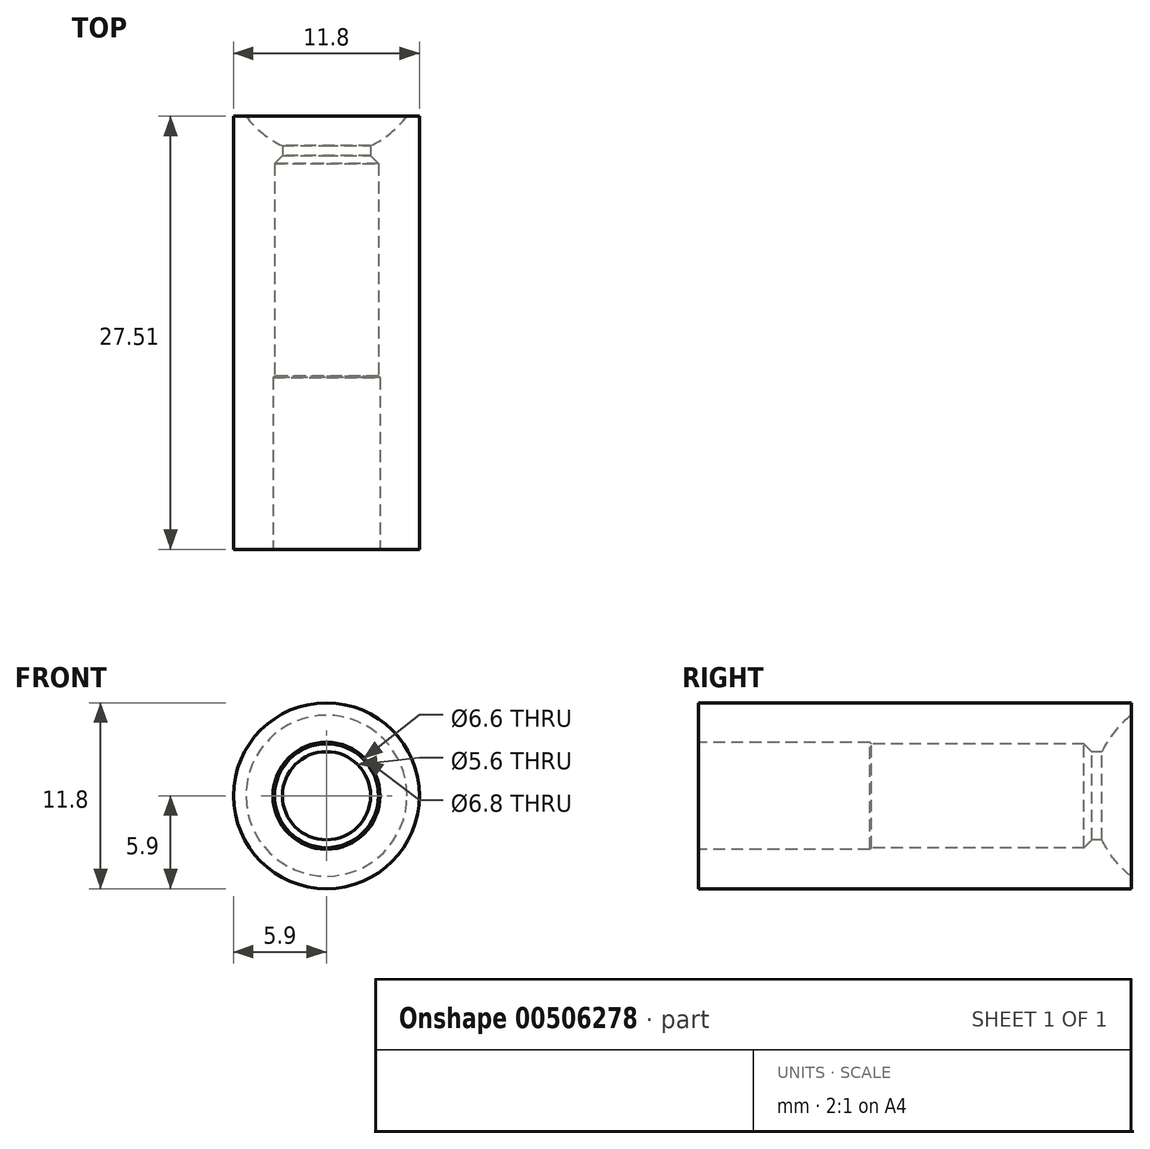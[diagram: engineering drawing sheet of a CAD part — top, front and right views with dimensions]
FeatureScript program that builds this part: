
annotation { "Feature Type Name" : "Feature", "Feature Type Description" : "" }
export const myFeature = defineFeature(function(context is Context, id is Id, definition is map)
    precondition{}
    {
        {
            var Q0;
            Q0=qCreatedBy(makeId("Right.planeOp"),FACE);
            var sketch = newSketch(context, id + "F0", { "sketchPlane" : qUnion([Q0])});
            skCircle(sketch, "E0", {"center": v(13.4, 0) * mm, "radius": 6.47 * mm});
            skLineSegment(sketch, "E1.bottom", {"start": v(6.43, -3.3) * mm, "end": v(-6.42, -3.3) * mm});
            skLineSegment(sketch, "E1.top", {"start": v(6.42, 3.3) * mm, "end": v(-6.43, 3.3) * mm});
            skLineSegment(sketch, "E1.left", {"start": v(6.43, -3.3) * mm, "end": v(6.43, 3.3) * mm});
            skLineSegment(sketch, "E1.right", {"start": v(-6.42, -3.3) * mm, "end": v(-6.43, 3.3) * mm});
            skPoint(sketch, "E1.middle", {"position": v(0, 0) * mm});
            skLineSegment(sketch, "E2.bottom", {"start": v(-18.07, -3.4) * mm, "end": v(-7.08, -3.4) * mm});
            skLineSegment(sketch, "E2.top", {"start": v(-18.07, 3.4) * mm, "end": v(-7.08, 3.4) * mm});
            skLineSegment(sketch, "E2.left", {"start": v(-18.07, -3.4) * mm, "end": v(-18.07, 3.4) * mm});
            skLineSegment(sketch, "E2.right", {"start": v(-7.08, -3.4) * mm, "end": v(-7.08, 3.4) * mm});
            skPoint(sketch, "E2.middle", {"position": v(-12.58, 0) * mm});
            skPoint(sketch, "E2.middle.positionSnap0", {"position": v(-6.42, 0) * mm});
            skPoint(sketch, "E2.centerSnap0", {"position": v(-6.42, 0) * mm});
            skLineSegment(sketch, "E3", {"start": v(0, 0) * mm, "end": v(4.23, 0) * mm, "construction": true});
            skLineSegment(sketch, "E4", {"start": v(6.42, 1.5) * mm, "end": v(7.1, 1.5) * mm});
            skLineSegment(sketch, "E5", {"start": v(-18.07, 3.4) * mm, "end": v(-18.07, 5.9) * mm});
            skLineSegment(sketch, "E6", {"start": v(-18.07, 5.9) * mm, "end": v(10.73, 5.9) * mm});
            skLineSegment(sketch, "E7", {"start": v(-6.43, 3.3) * mm, "end": v(-7.08, 3.3) * mm});
            skLineSegment(sketch, "E8", {"start": v(9.42, 5.9) * mm, "end": v(9.42, 5.11) * mm});
            skLineSegment(sketch, "E9", {"start": v(6.92, 0) * mm, "end": v(6.92, 3.3) * mm});
            skLineSegment(sketch, "E10", {"start": v(6.43, 3.3) * mm, "end": v(6.93, 2.8) * mm});
            skLineSegment(sketch, "E11", {"start": v(6.92, 3.3) * mm, "end": v(6.42, 3.3) * mm});
            skLineSegment(sketch, "E12", {"start": v(6.93, 2.8) * mm, "end": v(7.56, 2.8) * mm});
            skSolve(sketch);
        }
        {
            var Q0;
            Q0=makeQuery(id+"F0.imprint","IMPRINT",FACE,{"disambiguationData":[TD([[makeQuery(id+"F0.imprint","IMPRINT",EDGE,{"derivedFrom":sQuery(id+"F0.wireOp",EDGE,"E1.top")}),-1.0]])]});
            var Q1;
            {var subQ2=sQuery(id+"F0.wireOp",EDGE,"E10");Q1=makeQuery(id+"F0.imprint","IMPRINT",FACE,{"disambiguationData":[TD([[makeQuery(id+"F0.imprint","IMPRINT",EDGE,{"derivedFrom":subQ2}),1.0]])]});}
            var Q2;
            Q2=sQuery(id+"F0.wireOp",EDGE,"E3");
            revolve(context, id + "F1", {"entities" : qUnion([Q0, Q1]), "axis" : qUnion([Q2]), "revolveType" : RevolveType.FULL});
        }
        {
            var Q0;
            Q0=makeQuery(id+"F1.opRevolve","SWEPT_EDGE",EDGE,{"disambiguationData":[OSD([sQuery(id+"F0.wireOp",EDGE,"E2.top"),sQuery(id+"F0.wireOp",EDGE,"E2.right")])]});
            chamfer(context, id + "F2", {"entities" : qUnion([Q0]), "width" : 0.1 * mm, "tangentPropagation" : true});
        }
    });
